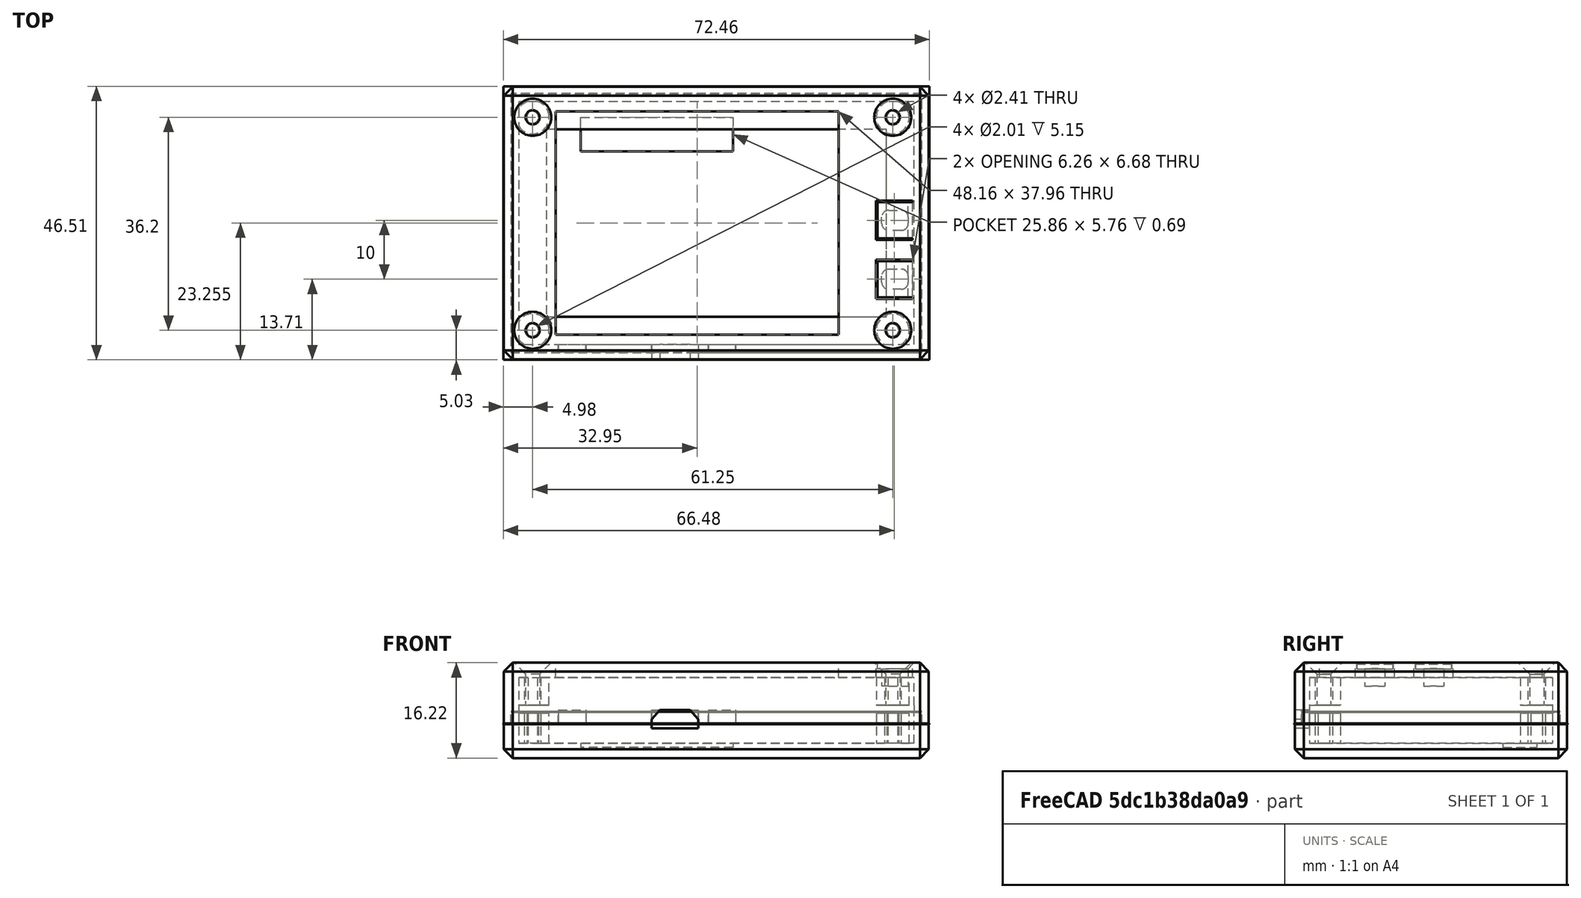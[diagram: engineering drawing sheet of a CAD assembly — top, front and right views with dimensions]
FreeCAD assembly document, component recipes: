
FREECAD ASSEMBLY — COMPONENT RECIPES ("case")

This assembly document has 4 components, labeled P0..P3 below (a component is one placed body or linked part). 2 of them carry a construction recipe — the FreeCAD feature program that regenerates the part from scratch, quoted from this document or its linked companion documents; the rest are supplied as boundary geometry only. No exploded tour is included for this assembly.
COMPONENT P0 — recipe-attached ("Body", modeled in this document).
Construction recipe (the document's own serialized feature program — sketch geometry with constraints, then the solid features built on it; lengths are millimeters unless a unit is written):

FEATURE [Sketcher::SketchObject] Sketch  label="OuterSketch"
  AttachmentOffset = pos=(0,0,-2.81) rot=(0,0,1;0rad)
  FullyConstrained = true
  MapMode = 5
  Placement = pos=(0,0,-2.81) rot=(0,0,1;0rad)
  Support = -> [XY_Plane]
  expr: .AttachmentOffset.Base.z = -(<<Param>>.T_WALL + <<Param>>.S_SIDE + <<Param>>.T_Z)
  expr: Constraints[10] = <<Param>>.T_WALL
  expr: Constraints[11] = <<Param>>.T_WALL
  expr: Constraints[7] = <<Param>>.W_BASE + 2 * (<<Param>>.T_WALL + <<Param>>.S_SIDE + <<Param>>.T_XY)
  expr: Constraints[8] = <<Param>>.H_BASE + 2 * (<<Param>>.T_WALL + <<Param>>.S_SIDE + <<Param>>.T_XY)
  sketch-geometry (4):
    g0: LineSegment StartX=-2.5 StartY=-2.5 StartZ=0 EndX=69.76 EndY=-2.5 EndZ=0
    g1: LineSegment StartX=69.76 StartY=-2.5 StartZ=0 EndX=69.76 EndY=43.81 EndZ=0
    g2: LineSegment StartX=69.76 StartY=43.81 StartZ=0 EndX=-2.5 EndY=43.81 EndZ=0
    g3: LineSegment StartX=-2.5 StartY=43.81 StartZ=0 EndX=-2.5 EndY=-2.5 EndZ=0
  constraints (12):
    c: Coincident(g0,g1)
    c: Coincident(g1,g2)
    c: Coincident(g2,g3)
    c: Horizontal(g0)
    c: Horizontal(g2)
    c: Vertical(g1)
    c: Vertical(g3)
    c: DistanceX(g0,g0) = 72.26
    c: DistanceY(g1,g1) = 46.31
    c: Coincident(g0,g3)
    c: DistanceX(g0,g-1) = 2.5
    c: DistanceY(g0,g-1) = 2.5
FEATURE [PartDesign::Pad] Pad  label="OuterPad"
  Direction = (0,0,1)
  Length = 16.22
  Length2 = 10
  Profile = -> Sketch
  ReferenceAxis = -> Sketch [N_Axis]
  Type = 0
  expr: Length = <<Param>>.D_BASE + 2 * (<<Param>>.T_WALL + <<Param>>.S_SIDE + <<Param>>.T_Z)
FEATURE [PartDesign::Chamfer] Chamfer  label="OuterChamfer"
  Angle = 45
  Base = -> Pad [Face6,Face1,Face5,Face2,Face3,Face4]
  BaseFeature = -> Pad
  ChamferType = 0
  FlipDirection = false
  Size = 1.5
  Size2 = 1
  SupportTransform = false
  UseAllEdges = true
  expr: Size = <<Param>>.R_CORNER
FEATURE [Sketcher::SketchObject] Sketch001  label="InnerSketch"
  AttachmentOffset = pos=(0,0,-0.31) rot=(0,0,1;0rad)
  FullyConstrained = true
  MapMode = 5
  Placement = pos=(0,0,-0.31) rot=(0,0,1;0rad)
  Support = -> [XY_Plane]
  expr: .AttachmentOffset.Base.z = -(<<Param>>.S_SIDE + <<Param>>.T_Z)
  expr: .Constraints.H1 = <<Param>>.H_BASE + 2 * (<<Param>>.S_SIDE + <<Param>>.T_XY)
  expr: .Constraints.W1 = <<Param>>.W_BASE + 2 * (<<Param>>.S_SIDE + <<Param>>.T_XY)
  sketch-geometry (4):
    g0: LineSegment StartX=0 StartY=0 StartZ=0 EndX=67.26 EndY=0 EndZ=0
    g1: LineSegment StartX=67.26 StartY=0 StartZ=0 EndX=67.26 EndY=41.31 EndZ=0
    g2: LineSegment StartX=67.26 StartY=41.31 StartZ=0 EndX=0 EndY=41.31 EndZ=0
    g3: LineSegment StartX=0 StartY=41.31 StartZ=0 EndX=0 EndY=0 EndZ=0
  constraints (11):
    c: Coincident(g0,g1)
    c: Coincident(g1,g2)
    c: Coincident(g2,g3)
    c: Coincident(g3,g0)
    c: Horizontal(g0)
    c: Horizontal(g2)
    c: Vertical(g1)
    c: Vertical(g3)
    c: Coincident(g0,g-1)
    c: DistanceX(g0,g0) = 67.26  'W1'
    c: DistanceY(g1,g1) = 41.31  'H1'
FEATURE [PartDesign::Pocket] Pocket  label="InnerPocket"
  BaseFeature = -> Chamfer
  Direction = (0,0,-1)
  Length = 11.22
  Length2 = 5
  Profile = -> Sketch001
  ReferenceAxis = -> Sketch001 [N_Axis]
  Reversed = true
  Type = 0
  expr: Length = <<Param>>.D_BASE + 2 * (<<Param>>.S_SIDE + <<Param>>.T_Z)
FEATURE [Sketcher::SketchObject] Sketch002  label="UpperScrewHolesSketch"
  AttachmentOffset = pos=(0,0,13.41) rot=(0,0,1;0rad)
  FullyConstrained = true
  MapMode = 5
  Placement = pos=(0,0,13.41) rot=(0,0,1;0rad)
  Support = -> [XY_Plane]
  expr: .AttachmentOffset.Base.z = <<Param>>.D_BASE + <<Param>>.S_SIDE + <<Param>>.T_WALL + <<Param>>.T_Z
  expr: .Constraints.X1 = <<SpacersSketch>>.Constraints.X1
  expr: .Constraints.Y1 = <<SpacersSketch>>.Constraints.Y1
  expr: Constraints[19] = <<Param>>.D_SCREW / 2
  expr: Constraints[8] = <<SpacersSketch>>.Constraints.W1
  expr: Constraints[9] = <<SpacersSketch>>.Constraints.H1
  sketch-geometry (8):
    g0: LineSegment StartX=2.38 StartY=2.43 StartZ=0 EndX=63.63 EndY=2.43 EndZ=0
    g1: LineSegment StartX=63.63 StartY=2.43 StartZ=0 EndX=63.63 EndY=38.63 EndZ=0
    g2: LineSegment StartX=63.63 StartY=38.63 StartZ=0 EndX=2.38 EndY=38.63 EndZ=0
    g3: LineSegment StartX=2.38 StartY=38.63 StartZ=0 EndX=2.38 EndY=2.43 EndZ=0
    g4: Circle CenterX=2.38 CenterY=38.63 CenterZ=0 NormalX=0 NormalY=0 NormalZ=1 AngleXU=0 Radius=1.125
    g5: Circle CenterX=63.63 CenterY=38.63 CenterZ=0 NormalX=0 NormalY=0 NormalZ=1 AngleXU=0 Radius=1.125
    g6: Circle CenterX=63.63 CenterY=2.43 CenterZ=0 NormalX=0 NormalY=0 NormalZ=1 AngleXU=0 Radius=1.125
    g7: Circle CenterX=2.38 CenterY=2.43 CenterZ=0 NormalX=0 NormalY=0 NormalZ=1 AngleXU=0 Radius=1.125
  constraints (20):
    c: Coincident(g0,g1)
    c: Coincident(g1,g2)
    c: Coincident(g2,g3)
    c: Coincident(g3,g0)
    c: Horizontal(g0)
    c: Horizontal(g2)
    c: Vertical(g1)
    c: Vertical(g3)
    c: DistanceX(g0,g0) = 61.25
    c: DistanceY(g1,g1) = 36.2
    c: DistanceX(g-1,g0) = 2.38  'X1'
    c: DistanceY(g-1,g0) = 2.43  'Y1'
    c: Coincident(g4,g2)
    c: Coincident(g5,g1)
    c: Coincident(g6,g0)
    c: Coincident(g7,g0)
    c: Equal(g4,g7)
    c: Equal(g7,g6)
    c: Equal(g6,g5)
    c: Radius(g4) = 1.125
FEATURE [Sketcher::SketchObject] Sketch003  label="SpacersSketch"
  AttachmentOffset = pos=(0,0,-0.31) rot=(0,0,1;0rad)
  FullyConstrained = true
  MapMode = 5
  Placement = pos=(0,0,-0.31) rot=(0,0,1;0rad)
  Support = -> [XY_Plane]
  expr: .AttachmentOffset.Base.z = <<InnerSketch>>.Placement.Base.z
  expr: .Constraints.H1 = 36.2 mm
  expr: .Constraints.W1 = 61.25 mm
  expr: .Constraints.X1 = 2.05 mm + <<Param>>.S_SIDE + <<Param>>.T_XY
  expr: .Constraints.Y1 = 2.1 mm + <<Param>>.S_SIDE + <<Param>>.T_XY
  expr: Constraints[19] = 2.8 mm
  sketch-geometry (8):
    g0: LineSegment StartX=2.38 StartY=2.43 StartZ=0 EndX=63.63 EndY=2.43 EndZ=0
    g1: LineSegment StartX=63.63 StartY=2.43 StartZ=0 EndX=63.63 EndY=38.63 EndZ=0
    g2: LineSegment StartX=63.63 StartY=38.63 StartZ=0 EndX=2.38 EndY=38.63 EndZ=0
    g3: LineSegment StartX=2.38 StartY=38.63 StartZ=0 EndX=2.38 EndY=2.43 EndZ=0
    g4: Circle CenterX=2.38 CenterY=38.63 CenterZ=0 NormalX=0 NormalY=0 NormalZ=1 AngleXU=0 Radius=2.8
    g5: Circle CenterX=63.63 CenterY=38.63 CenterZ=0 NormalX=0 NormalY=0 NormalZ=1 AngleXU=0 Radius=2.8
    g6: Circle CenterX=63.63 CenterY=2.43 CenterZ=0 NormalX=0 NormalY=0 NormalZ=1 AngleXU=0 Radius=2.8
    g7: Circle CenterX=2.38 CenterY=2.43 CenterZ=0 NormalX=0 NormalY=0 NormalZ=1 AngleXU=0 Radius=2.8
  constraints (20):
    c: Coincident(g0,g1)
    c: Coincident(g1,g2)
    c: Coincident(g2,g3)
    c: Coincident(g3,g0)
    c: Horizontal(g0)
    c: Horizontal(g2)
    c: Vertical(g1)
    c: Vertical(g3)
    c: DistanceX(g0,g0) = 61.25  'W1'
    c: DistanceY(g1,g1) = 36.2  'H1'
    c: DistanceX(g-1,g0) = 2.38  'X1'
    c: DistanceY(g-1,g0) = 2.43  'Y1'
    c: Coincident(g4,g2)
    c: Coincident(g5,g1)
    c: Coincident(g6,g0)
    c: Coincident(g7,g0)
    c: Equal(g4,g7)
    c: Equal(g7,g6)
    c: Equal(g6,g5)
    c: Radius(g4) = 2.8
FEATURE [PartDesign::Pad] Pad001  label="SpacersPad"
  BaseFeature = -> Pocket
  Direction = (0,0,1)
  Length = 11.22
  Length2 = 10
  Profile = -> Sketch003
  ReferenceAxis = -> Sketch003 [N_Axis]
  Type = 0
  expr: Length = <<InnerPocket>>.Length
FEATURE [PartDesign::SubShapeBinder] Binder  label="InnerSketchBinder"
  BindCopyOnChange = 0
  BindMode = 0
  ClaimChildren = false
  Context = -> Body [Binder.]
  Fuse = false
  MakeFace = true
  OffsetFill = false
  OffsetIntersection = false
  OffsetJoinType = 0
  OffsetOpenResult = false
  PartialLoad = false
  Placement = pos=(0,0,6.47) rot=(0,0,1;0rad)
  Relative = true
  Support = -> [Pocket[Sketch001.]]
  _Version = 2
  expr: .Placement.Base.z = <<InnerPocket>>.Length - <<Param>>.S_SIDE - <<Param>>.Y_TOP
FEATURE [Sketcher::SketchObject] Sketch005  label="ScreenBaseSketch"
  AttachmentOffset = pos=(0,0,6.47) rot=(0,0,1;0rad)
  FullyConstrained = true
  MapMode = 5
  Placement = pos=(0,0,6.47) rot=(0,0,1;0rad)
  Support = -> [XY_Plane]
  expr: .AttachmentOffset.Base.z = <<InnerSketchBinder>>.Placement.Base.z
  expr: Constraints[19] = <<InnerSketch>>.Constraints.W1
  expr: Constraints[20] = <<InnerSketch>>.Constraints.H1
  expr: Constraints[24] = <<UpperScrewHolesSketch>>.Constraints.X1 + 0.9 mm
  expr: Constraints[8] = <<Param>>.W_SCREEN + 2 * <<Param>>.T_XY
  expr: Constraints[9] = <<Param>>.H_SCREEN + 2 * <<Param>>.T_XY
  sketch-geometry (10):
    g0: LineSegment StartX=6.27 StartY=1.675 StartZ=0 EndX=54.43 EndY=1.675 EndZ=0
    g1: LineSegment StartX=54.43 StartY=1.675 StartZ=0 EndX=54.43 EndY=39.635 EndZ=0
    g2: LineSegment StartX=54.43 StartY=39.635 StartZ=0 EndX=6.27 EndY=39.635 EndZ=0
    g3: LineSegment StartX=6.27 StartY=39.635 StartZ=0 EndX=6.27 EndY=1.675 EndZ=0
    g4: LineSegment StartX=0 StartY=0 StartZ=0 EndX=67.26 EndY=0 EndZ=0
    g5: LineSegment StartX=67.26 StartY=0 StartZ=0 EndX=67.26 EndY=41.31 EndZ=0
    g6: LineSegment StartX=67.26 StartY=41.31 StartZ=0 EndX=0 EndY=41.31 EndZ=0
    g7: LineSegment StartX=0 StartY=41.31 StartZ=0 EndX=0 EndY=0 EndZ=0
    g8: GeomPoint X=33.63 Y=20.655 Z=0
    g9: GeomPoint X=30.35 Y=20.655 Z=0
  constraints (25):
    c: Coincident(g0,g1)
    c: Coincident(g1,g2)
    c: Coincident(g2,g3)
    c: Coincident(g3,g0)
    c: Horizontal(g0)
    c: Horizontal(g2)
    c: Vertical(g1)
    c: Vertical(g3)
    c: DistanceX(g0,g0) = 48.16
    c: DistanceY(g1,g1) = 37.96
    c: Coincident(g4,g5)
    c: Coincident(g5,g6)
    c: Coincident(g6,g7)
    c: Coincident(g7,g4)
    c: Horizontal(g4)
    c: Horizontal(g6)
    c: Vertical(g5)
    c: Vertical(g7)
    c: Coincident(g4,g-1)
    c: DistanceX(g4,g4) = 67.26
    c: DistanceY(g5,g5) = 41.31
    c: Symmetric(g4,g5,g8)
    c: Symmetric(g0,g1,g9)
    c: Horizontal(g9,g8)
    c: DistanceX(g9,g8) = 3.28
FEATURE [PartDesign::Hole] Hole  label="UpperScrewHoles"
  BaseFeature = -> Pad001
  CustomThreadClearance = 0
  Depth = 7.31
  DepthType = 0
  Diameter = 2.41
  DrillForDepth = false
  DrillPoint = 0
  DrillPointAngle = 118
  HoleCutCountersinkAngle = 90
  HoleCutCustomValues = false
  HoleCutDepth = 0
  HoleCutDiameter = 6.3
  HoleCutType = 2
  ModelThread = false
  Profile = -> Sketch002
  Tapered = false
  TaperedAngle = 90
  ThreadClass = 0
  ThreadDepth = 7.31
  ThreadDepthType = 0
  ThreadDirection = 0
  ThreadFit = 1
  ThreadSize = 0
  ThreadType = 0
  Threaded = false
  UseCustomThreadClearance = false
  expr: Depth = <<Param>>.T_WALL + <<Param>>.S_SIDE + <<Param>>.T_Z + <<Param>>.Y_TOP
  expr: Diameter = <<Param>>.D_SCREW + 2 * <<Param>>.T_XY
FEATURE [PartDesign::Hole] Hole001  label="InnerScrewHoles"
  BaseFeature = -> Hole
  CustomThreadClearance = 0
  Depth = 13.72
  DepthType = 0
  Diameter = 2.01
  DrillForDepth = false
  DrillPoint = 0
  DrillPointAngle = 118
  HoleCutCountersinkAngle = 90
  HoleCutCustomValues = false
  HoleCutDepth = 0
  HoleCutDiameter = 6.1
  HoleCutType = 0
  ModelThread = false
  Profile = -> Sketch002
  Tapered = false
  TaperedAngle = 90
  ThreadClass = 0
  ThreadDepth = 13.72
  ThreadDepthType = 0
  ThreadDirection = 0
  ThreadFit = 0
  ThreadSize = 0
  ThreadType = 0
  Threaded = false
  UseCustomThreadClearance = false
  expr: Depth = <<Param>>.T_WALL + <<InnerPocket>>.Length
  expr: Diameter = <<Param>>.D_SCREW - 0.4 mm + 2 * <<Param>>.T_XY
FEATURE [PartDesign::Pocket] Pocket002  label="PcbPocket"
  BaseFeature = -> Hole001
  Direction = (0,0,-1)
  Length = 1.32
  Length2 = 5
  Profile = -> Binder
  Type = 0
  expr: Length = <<Param>>.T_PCB + 2 * <<Param>>.T_Z
FEATURE [PartDesign::Pocket] Pocket003  label="ScreenBasePocket"
  BaseFeature = -> Pocket002
  Direction = (0,0,-1)
  Length = 5
  Length2 = 5
  Profile = -> Sketch005
  ReferenceAxis = -> Sketch005 [N_Axis]
  Reversed = true
  Type = 1
FEATURE [Sketcher::SketchObject] Sketch006  label="TasterSketch"
  AttachmentOffset = pos=(0,0,5.33) rot=(0,0,1;0rad)
  FullyConstrained = true
  MapMode = 5
  Placement = pos=(0,0,5.33) rot=(0,0,1;0rad)
  Support = -> [XY_Plane]
  expr: .AttachmentOffset.Base.z = <<InnerSketchBinder>>.Placement.Base.z - <<Param>>.T_PCB + <<Param>>.T_Z
  expr: Constraints[10] = 4.5 mm + 2 * <<Param>>.T_XY
  expr: Constraints[11] = 1.2 mm + <<Param>>.T_XY
  expr: Constraints[23] = 32 mm + <<Param>>.S_SIDE
  expr: Constraints[9] = 6.5 mm + <<Param>>.S_SIDE
  sketch-geometry (8):
    g0: LineSegment StartX=6.75 StartY=0 StartZ=0 EndX=11.41 EndY=0 EndZ=0
    g1: LineSegment StartX=11.41 StartY=0 StartZ=0 EndX=11.41 EndY=-1.28 EndZ=0
    g2: LineSegment StartX=11.41 StartY=-1.28 StartZ=0 EndX=6.75 EndY=-1.28 EndZ=0
    g3: LineSegment StartX=6.75 StartY=-1.28 StartZ=0 EndX=6.75 EndY=0 EndZ=0
    g4: LineSegment StartX=32.25 StartY=0 StartZ=0 EndX=36.91 EndY=0 EndZ=0
    g5: LineSegment StartX=36.91 StartY=0 StartZ=0 EndX=36.91 EndY=-1.28 EndZ=0
    g6: LineSegment StartX=36.91 StartY=-1.28 StartZ=0 EndX=32.25 EndY=-1.28 EndZ=0
    g7: LineSegment StartX=32.25 StartY=-1.28 StartZ=0 EndX=32.25 EndY=0 EndZ=0
  constraints (24):
    c: Coincident(g0,g1)
    c: Coincident(g1,g2)
    c: Coincident(g2,g3)
    c: Coincident(g3,g0)
    c: Horizontal(g0)
    c: Horizontal(g2)
    c: Vertical(g1)
    c: Vertical(g3)
    c: PointOnObject(g0,g-1)
    c: DistanceX(g0) = 6.75
    c: DistanceX(g0,g0) = 4.66
    c: DistanceY(g1,g1) = 1.28
    c: Coincident(g4,g5)
    c: Coincident(g5,g6)
    c: Coincident(g6,g7)
    c: Coincident(g7,g4)
    c: Horizontal(g4)
    c: Horizontal(g6)
    c: Vertical(g5)
    c: Vertical(g7)
    c: PointOnObject(g4,g-1)
    c: Horizontal(g1,g6)
    c: Equal(g4,g0)
    c: DistanceX(g4) = 32.25
FEATURE [Sketcher::SketchObject] Sketch007  label="UsbSketch"
  FullyConstrained = true
  MapMode = 5
  Placement = pos=(0,0,0) rot=(1,0,0;1.5708rad)
  Support = -> [XZ_Plane]
  expr: .Constraints.H1 = 3 mm + 2 * <<Param>>.T_Z
  expr: .Constraints.W1 = 7.8 mm + 2 * <<Param>>.T_XY
  expr: .Constraints.X1 = 22.34 mm + <<Param>>.S_SIDE
  expr: .Constraints.Y1 = <<InnerSketchBinder>>.Placement.Base.z - <<Param>>.T_PCB + 0.1 mm
  expr: Constraints[22] = 5 mm + 2 * <<Param>>.T_XY
  expr: Constraints[27] = 1.5 mm
  sketch-geometry (10):
    g0: LineSegment StartX=29.15 StartY=5.37 StartZ=0 EndX=23.99 EndY=5.37 EndZ=0
    g1: LineSegment StartX=23.99 StartY=5.37 StartZ=0 EndX=22.59 EndY=3.75 EndZ=0
    g2: LineSegment StartX=22.59 StartY=3.75 StartZ=0 EndX=22.59 EndY=2.25 EndZ=0
    g3: LineSegment StartX=22.59 StartY=2.25 StartZ=0 EndX=30.55 EndY=2.25 EndZ=0
    g4: LineSegment StartX=30.55 StartY=2.25 StartZ=0 EndX=30.55 EndY=3.75 EndZ=0
    g5: LineSegment StartX=30.55 StartY=3.75 StartZ=0 EndX=29.15 EndY=5.37 EndZ=0
    g6: LineSegment StartX=22.59 StartY=3.75 StartZ=0 EndX=23.99 EndY=3.75 EndZ=0
    g7: LineSegment StartX=23.99 StartY=3.75 StartZ=0 EndX=29.15 EndY=3.75 EndZ=0
    g8: LineSegment StartX=29.15 StartY=3.75 StartZ=0 EndX=30.55 EndY=3.75 EndZ=0
    g9: GeomPoint X=22.59 Y=5.37 Z=0
  constraints (28):
    c: Horizontal(g0)
    c: Coincident(g0,g1)
    c: Coincident(g1,g2)
    c: Vertical(g2)
    c: Coincident(g2,g3)
    c: Horizontal(g3)
    c: Coincident(g3,g4)
    c: Vertical(g4)
    c: Coincident(g4,g5)
    c: Coincident(g5,g0)
    c: Horizontal(g1,g4)
    c: Coincident(g6,g1)
    c: Horizontal(g6)
    c: Coincident(g7,g6)
    c: Horizontal(g7)
    c: Coincident(g8,g7)
    c: Coincident(g8,g4)
    c: Vertical(g0,g7)
    c: Vertical(g0,g6)
    c: Equal(g8,g6)
    c: DistanceY(g3,g0) = 3.12  'H1'
    c: DistanceX(g3,g3) = 7.96  'W1'
    c: DistanceX(g0,g0) = 5.16
    c: Vertical(g9,g1)
    c: Horizontal(g9,g0)
    c: DistanceX(g9) = 22.59  'X1'
    c: DistanceY(g9) = 5.37  'Y1'
    c: DistanceY(g2,g2) = 1.5
FEATURE [Sketcher::SketchObject] Sketch008  label="ButtonSketch"
  AttachmentOffset = pos=(0,0,0.25) rot=(0,0,1;0rad)
  FullyConstrained = true
  MapMode = 5
  Placement = pos=(0,0,0.25) rot=(0,0,1;0rad)
  Support = -> [XY_Plane]
  expr: .AttachmentOffset.Base.z = <<Param>>.S_SIDE
  expr: .Constraints.H1 = 6 mm + 2 * <<Param>>.T_XY
  expr: .Constraints.W1 = 6 mm
  expr: .Constraints.X1 = <<InnerSketch>>.Constraints.W1 - <<Param>>.S_SIDE
  expr: .Constraints.Y1 = 7.7 mm + <<Param>>.S_SIDE + <<Param>>.T_XY
  expr: .Constraints.Y2 = .Constraints.H1 + 0.1 mm + 2 * <<Param>>.T_XY
  expr: Constraints[25] = .Constraints.Y2
  sketch-geometry (9):
    g0: LineSegment StartX=60.75 StartY=14.45 StartZ=0 EndX=67.01 EndY=14.45 EndZ=0
    g1: LineSegment StartX=67.01 StartY=14.45 StartZ=0 EndX=67.01 EndY=14.19 EndZ=0
    g2: LineSegment StartX=67.01 StartY=7.77 StartZ=0 EndX=60.75 EndY=7.77 EndZ=0
    g3: LineSegment StartX=60.75 StartY=7.77 StartZ=0 EndX=60.75 EndY=14.45 EndZ=0
    g4: LineSegment StartX=61.01 StartY=14.19 StartZ=0 EndX=67.01 EndY=14.19 EndZ=0
    g5: LineSegment StartX=67.01 StartY=8.03 StartZ=0 EndX=61.01 EndY=8.03 EndZ=0
    g6: LineSegment StartX=61.01 StartY=8.03 StartZ=0 EndX=61.01 EndY=14.19 EndZ=0
    g7: LineSegment StartX=67.01 StartY=8.03 StartZ=0 EndX=67.01 EndY=7.77 EndZ=0
    g8: LineSegment StartX=61.01 StartY=8.03 StartZ=0 EndX=60.75 EndY=8.03 EndZ=0
  constraints (29):
    c: Coincident(g0,g1)
    c: Coincident(g7,g2)
    c: Coincident(g2,g3)
    c: Coincident(g3,g0)
    c: Horizontal(g0)
    c: Horizontal(g2)
    c: Vertical(g1)
    c: Vertical(g3)
    c: Coincident(g5,g6)
    c: Coincident(g6,g4)
    c: Horizontal(g4)
    c: Horizontal(g5)
    c: Vertical(g6)
    c: Coincident(g4,g1)
    c: Coincident(g5,g7)
    c: Vertical(g1,g5)
    c: Coincident(g8,g5)
    c: PointOnObject(g8,g3)
    c: Horizontal(g8)
    c: DistanceY(g6,g6) = 6.16  'H1'
    c: DistanceX(g5,g5) = 6  'W1'
    c: Vertical(g7)
    c: DistanceY(g2,g1) = 6.42  'Y2'
    c: DistanceX(g5) = 67.01  'X1'
    c: DistanceY(g5) = 8.03  'Y1'
    c: DistanceY(g5,g0) = 6.42
    c: Equal(g7,g8)
    c: DistanceY(g3,g3) = 6.68  'H2'
    c: DistanceX(g2,g2) = 6.26  'W2'
FEATURE [Sketcher::SketchObject] Sketch009  label="ButtonPeerSketch"
  AttachmentOffset = pos=(0,0,13.41) rot=(0,0,1;0rad)
  FullyConstrained = false
  MapMode = 5
  Placement = pos=(0,0,13.41) rot=(0,0,1;0rad)
  Support = -> [XY_Plane]
  expr: .AttachmentOffset.Base.z = <<OuterSketch>>.Placement.Base.z + <<OuterPad>>.Length
  expr: Constraints[10] = <<ButtonSketch>>.Constraints.W1
  expr: Constraints[11] = <<ButtonSketch>>.Constraints.H1
  expr: Constraints[34] = 3.4 mm
  expr: Constraints[36] = 4.5 mm
  expr: Constraints[8] = <<ButtonSketch>>.Constraints.X1 - <<Param>>.S_SIDE - 0.5 mm
  expr: Constraints[9] = <<ButtonSketch>>.Constraints.Y1
  sketch-geometry (15):
    g0: LineSegment StartX=60.26 StartY=14.19 StartZ=0 EndX=66.26 EndY=14.19 EndZ=0
    g1: LineSegment StartX=66.26 StartY=14.19 StartZ=0 EndX=66.26 EndY=8.03 EndZ=0
    g2: LineSegment StartX=66.26 StartY=8.03 StartZ=0 EndX=60.26 EndY=8.03 EndZ=0
    g3: LineSegment StartX=60.26 StartY=8.03 StartZ=0 EndX=60.26 EndY=14.19 EndZ=0
    g4: ArcOfCircle CenterX=62.9093 CenterY=11.6607 CenterZ=0 NormalX=0 NormalY=0 NormalZ=1 AngleXU=0 Radius=1.14926 StartAngle=1.5708 EndAngle=3.14159
    g5: LineSegment StartX=62.9093 StartY=12.81 StartZ=0 EndX=65.1107 EndY=12.81 EndZ=0
    g6: ArcOfCircle CenterX=65.1107 CenterY=11.6607 CenterZ=0 NormalX=0 NormalY=0 NormalZ=1 AngleXU=0 Radius=1.14926 StartAngle=0 EndAngle=1.5708
    g7: LineSegment StartX=66.26 StartY=11.6607 StartZ=0 EndX=66.26 EndY=10.5593 EndZ=0
    g8: ArcOfCircle CenterX=65.1107 CenterY=10.5593 CenterZ=0 NormalX=0 NormalY=0 NormalZ=1 AngleXU=0 Radius=1.14926 StartAngle=4.71239 EndAngle=6.28319
    g9: LineSegment StartX=65.1107 StartY=9.41 StartZ=0 EndX=62.9093 EndY=9.41 EndZ=0
    g10: ArcOfCircle CenterX=62.9093 CenterY=10.5593 CenterZ=0 NormalX=0 NormalY=0 NormalZ=1 AngleXU=0 Radius=1.14926 StartAngle=3.14159 EndAngle=4.71239
    g11: LineSegment StartX=61.76 StartY=10.5593 StartZ=0 EndX=61.76 EndY=11.6607 EndZ=0
    g12: GeomPoint X=61.76 Y=12.81 Z=0
    g13: GeomPoint X=66.26 Y=9.41 Z=0
    g14: LineSegment StartX=64.01 StartY=11.11 StartZ=0 EndX=66.26 EndY=11.11 EndZ=0
  constraints (37):
    c: Coincident(g0,g1)
    c: Coincident(g1,g2)
    c: Coincident(g2,g3)
    c: Coincident(g3,g0)
    c: Horizontal(g0)
    c: Horizontal(g2)
    c: Vertical(g1)
    c: Vertical(g3)
    c: DistanceX(g1) = 66.26
    c: DistanceY(g1) = 8.03
    c: DistanceX(g2,g2) = 6
    c: DistanceY(g1,g1) = 6.16
    c: Tangent(g4,g5) = 1.5708
    c: Tangent(g5,g6) = 1.5708
    c: Tangent(g6,g7) = 1.5708
    c: Tangent(g7,g8) = 1.5708
    c: Tangent(g8,g9) = 1.5708
    c: Tangent(g9,g10) = 1.5708
    c: Tangent(g10,g11) = 1.5708
    c: Tangent(g11,g4) = 1.5708
    c: Horizontal(g5)
    c: Horizontal(g9)
    c: Vertical(g7)
    c: Vertical(g11)
    c: Equal(g4,g6)
    c: Equal(g6,g8)
    c: Equal(g8,g10)
    c: PointOnObject(g12,g5)
    c: PointOnObject(g12,g11)
    c: PointOnObject(g13,g7)
    c: PointOnObject(g13,g9)
    c: Horizontal(g14)
    c: Symmetric(g4,g8,g14)
    c: Symmetric(g1,g0,g14)
    c: DistanceY(g9,g4) = 3.4
    c: Vertical(g6,g0)
    c: DistanceX(g10,g7) = 4.5
FEATURE [Sketcher::SketchObject] Sketch011  label="InnerUsbSketch"
  FullyConstrained = true
  MapMode = 5
  Placement = pos=(0,0,0) rot=(1,0,0;1.5708rad)
  Support = -> [XZ_Plane]
  expr: Constraints[10] = <<UsbSketch>>.Constraints.W1
  expr: Constraints[11] = <<UsbSketch>>.Constraints.H1
  expr: Constraints[8] = <<UsbSketch>>.Constraints.X1
  expr: Constraints[9] = <<UsbSketch>>.Constraints.Y1
  sketch-geometry (4):
    g0: LineSegment StartX=22.59 StartY=5.37 StartZ=0 EndX=30.55 EndY=5.37 EndZ=0
    g1: LineSegment StartX=30.55 StartY=5.37 StartZ=0 EndX=30.55 EndY=2.25 EndZ=0
    g2: LineSegment StartX=30.55 StartY=2.25 StartZ=0 EndX=22.59 EndY=2.25 EndZ=0
    g3: LineSegment StartX=22.59 StartY=2.25 StartZ=0 EndX=22.59 EndY=5.37 EndZ=0
  constraints (12):
    c: Coincident(g0,g1)
    c: Coincident(g1,g2)
    c: Coincident(g2,g3)
    c: Coincident(g3,g0)
    c: Horizontal(g0)
    c: Horizontal(g2)
    c: Vertical(g1)
    c: Vertical(g3)
    c: DistanceX(g0) = 22.59
    c: DistanceY(g0) = 5.37
    c: DistanceX(g0,g0) = 7.96
    c: DistanceY(g1,g1) = 3.12
FEATURE [Sketcher::SketchObject] Sketch012  label="ButtonCarveSketch"
  AttachmentOffset = pos=(0,0,-8.03) rot=(0,0,1;0rad)
  FullyConstrained = true
  MapMode = 5
  Placement = pos=(0,8.03,1.8e-15) rot=(1,0,0;1.5708rad)
  Support = -> [XZ_Plane]
  expr: .AttachmentOffset.Base.z = -<<ButtonSketch>>.Constraints.Y1
  expr: .Constraints.Y1 = <<InnerPocket>>.Length - <<Param>>.S_SIDE - <<Param>>.T_Z
  expr: .Constraints.Y2 = <<InnerPocket>>.Length - <<Param>>.S_SIDE - 2 * <<Param>>.T_Z + <<Param>>.T_WALL - <<Param>>.T_BUTTON
  expr: .Constraints.Y3 = <<InnerPocket>>.Length - <<Param>>.S_SIDE - 2 * <<Param>>.T_Z + <<Param>>.T_WALL - <<Param>>.T_LAYER
  expr: Constraints[10] = <<ButtonSketch>>.Constraints.X1
  expr: Constraints[14] = <<ButtonSketch>>.Constraints.W2
  sketch-geometry (5):
    g0: LineSegment StartX=66.21 StartY=12.35 StartZ=0 EndX=60.75 EndY=12.35 EndZ=0
    g1: LineSegment StartX=60.75 StartY=12.35 StartZ=0 EndX=60.75 EndY=10.91 EndZ=0
    g2: LineSegment StartX=60.75 StartY=10.91 StartZ=0 EndX=67.01 EndY=10.91 EndZ=0
    g3: LineSegment StartX=67.01 StartY=10.91 StartZ=0 EndX=67.01 EndY=13.15 EndZ=0
    g4: LineSegment StartX=67.01 StartY=13.15 StartZ=0 EndX=66.21 EndY=12.35 EndZ=0
  constraints (15):
    c: Horizontal(g0)
    c: Coincident(g0,g1)
    c: Vertical(g1)
    c: Coincident(g1,g2)
    c: Horizontal(g2)
    c: Coincident(g2,g3)
    c: Vertical(g3)
    c: Coincident(g3,g4)
    c: Coincident(g4,g0)
    c: Angle(g4,g3) = 0.785398
    c: DistanceX(g2) = 67.01
    c: DistanceY(g0) = 12.35  'Y2'
    c: DistanceY(g3) = 13.15  'Y3'
    c: DistanceY(g1) = 10.91  'Y1'
    c: DistanceX(g2,g2) = 6.26
FEATURE [Sketcher::SketchObject] Sketch013  label="PinHeaderSketch"
  FullyConstrained = true
  MapMode = 5
  Support = -> [XY_Plane]
  expr: Constraints[10] = 5.1 mm + 2 * (<<Param>>.S_SIDE + <<Param>>.T_XY)
  expr: Constraints[11] = 25.2 mm + 2 * (<<Param>>.S_SIDE + <<Param>>.T_XY)
  expr: Constraints[8] = 10.9 mm - <<Param>>.S_SIDE - <<Param>>.T_XY
  expr: Constraints[9] = 33.2 mm - <<Param>>.S_SIDE - <<Param>>.T_XY
  sketch-geometry (4):
    g0: LineSegment StartX=10.57 StartY=38.63 StartZ=0 EndX=36.43 EndY=38.63 EndZ=0
    g1: LineSegment StartX=36.43 StartY=38.63 StartZ=0 EndX=36.43 EndY=32.87 EndZ=0
    g2: LineSegment StartX=36.43 StartY=32.87 StartZ=0 EndX=10.57 EndY=32.87 EndZ=0
    g3: LineSegment StartX=10.57 StartY=32.87 StartZ=0 EndX=10.57 EndY=38.63 EndZ=0
  constraints (12):
    c: Coincident(g0,g1)
    c: Coincident(g1,g2)
    c: Coincident(g2,g3)
    c: Coincident(g3,g0)
    c: Horizontal(g0)
    c: Horizontal(g2)
    c: Vertical(g1)
    c: Vertical(g3)
    c: DistanceX(g2) = 10.57
    c: DistanceY(g2) = 32.87
    c: DistanceY(g1,g1) = 5.76
    c: DistanceX(g0,g0) = 25.86
FEATURE [PartDesign::Pocket] Pocket009  label="PinHeaderPocket"
  BaseFeature = -> Pocket003
  Direction = (0,0,-1)
  Length = 1
  Length2 = 5
  Profile = -> Sketch013
  ReferenceAxis = -> Sketch013 [N_Axis]
  Type = 0
FEATURE [PartDesign::Pocket] Pocket004  label="TasterPocket"
  BaseFeature = -> Pocket009
  Direction = (0,0,-1)
  Length = 2.47
  Length2 = 5
  Profile = -> Sketch006
  ReferenceAxis = -> Sketch006 [N_Axis]
  Type = 0
  expr: Length = 2.35 mm + 2 * <<Param>>.T_Z
FEATURE [PartDesign::Pocket] Pocket005  label="UsbPocket"
  BaseFeature = -> Pocket004
  Direction = (0,1,2e-16)
  Length = 5
  Length2 = 5
  Profile = -> Sketch007
  ReferenceAxis = -> Sketch007 [N_Axis]
  Reversed = true
  Type = 1
FEATURE [PartDesign::Pocket] Pocket007  label="InnerUsbPocket"
  BaseFeature = -> Pocket005
  Direction = (0,1,2e-16)
  Length = 1.33
  Length2 = 5
  Profile = -> Sketch011
  ReferenceAxis = -> Sketch011 [N_Axis]
  Reversed = true
  Type = 0
  expr: Length = <<Param>>.T_WALL / 2 + <<Param>>.T_XY
FEATURE [PartDesign::Pocket] Pocket006  label="ButtonPocket"
  BaseFeature = -> Pocket007
  Direction = (0,0,-1)
  Length = 5
  Length2 = 5
  Profile = -> Sketch008
  ReferenceAxis = -> Sketch008 [N_Axis]
  Reversed = true
  Type = 1
FEATURE [PartDesign::Pocket] Pocket008  label="ButtonCarvePocket"
  BaseFeature = -> Pocket006
  Direction = (0,1,2e-16)
  Length = 6.16
  Length2 = 5
  Profile = -> Sketch012
  ReferenceAxis = -> Sketch012 [N_Axis]
  Type = 0
  expr: Length = <<ButtonSketch>>.Constraints.H1
FEATURE [PartDesign::Pad] Pad002  label="ButtonPeerPad"
  BaseFeature = -> Pocket008
  Direction = (0,0,1)
  Length = 4
  Length2 = 10
  Profile = -> Sketch009
  ReferenceAxis = -> Sketch009 [N_Axis]
  Reversed = true
  Type = 0
  expr: Length = <<Param>>.T_WALL + <<Param>>.S_SIDE + 1.25 mm
FEATURE [PartDesign::LinearPattern] LinearPattern  label="ButtonLinearPattern"
  BaseFeature = -> Pad002
  Direction = -> Y_Axis
  Length = 10
  Occurrences = 2
  Originals = -> [Pocket006,Pocket008,Pad002]
FEATURE [PartDesign::Body] Body
  Group = -> [Sketch,Pad,Chamfer,Sketch001,Pocket,Sketch002,Sketch003,Pad001,Hole,Hole001,Binder,Pocket002,Sketch005,Pocket003,Sketch006,Sketch013,Pocket009,Pocket004,Sketch007,Pocket005,Sketch008,Sketch011,Pocket007,Pocket006,Sketch009,Sketch012,Pocket008,Pad002,LinearPattern]
  Origin = -> Origin
  Tip = -> LinearPattern
COMPONENT P1 — recipe-attached ("Gap", modeled in this document).
Construction recipe (the document's own serialized feature program — sketch geometry with constraints, then the solid features built on it; lengths are millimeters unless a unit is written):

FEATURE [Sketcher::SketchObject] Sketch010  label="GapSketch"
  AttachmentOffset = pos=(0,0,-20.655) rot=(0,0,1;0rad)
  FullyConstrained = true
  MapMode = 5
  Placement = pos=(0,20.655,4.6e-15) rot=(1,0,0;1.5708rad)
  Support = -> [XZ_Plane001]
  expr: .AttachmentOffset.Base.z = -<<InnerSketch>>.Constraints.H1 / 2
  expr: .Constraints.Y1 = <<InnerSketchBinder>>.Placement.Base.z - <<Param>>.S_SIDE - <<Param>>.T_PCB + <<Param>>.T_Z
  expr: .Constraints.Y2 = .Constraints.Y1 - 2 * <<Param>>.T_Z
  expr: Constraints[16] = -<<Param>>.T_WALL - 0.1 mm
  expr: Constraints[26] = <<Param>>.T_XY
  expr: Constraints[27] = <<Param>>.H_LATCH
  sketch-geometry (9):
    g0: LineSegment StartX=4.725 StartY=5.08 StartZ=0 EndX=-1.355 EndY=5.08 EndZ=0
    g1: LineSegment StartX=-1.355 StartY=5.08 StartZ=0 EndX=-1.355 EndY=3.08 EndZ=0
    g2: LineSegment StartX=-1.355 StartY=3.08 StartZ=0 EndX=-2.6 EndY=3.08 EndZ=0
    g3: LineSegment StartX=-2.6 StartY=3.08 StartZ=0 EndX=-2.6 EndY=2.96 EndZ=0
    g4: LineSegment StartX=-2.6 StartY=2.96 StartZ=0 EndX=-1.275 EndY=2.96 EndZ=0
    g5: LineSegment StartX=-1.275 StartY=2.96 StartZ=0 EndX=-1.275 EndY=4.96 EndZ=0
    g6: LineSegment StartX=-1.275 StartY=4.96 StartZ=0 EndX=4.725 EndY=4.96 EndZ=0
    g7: LineSegment StartX=4.725 StartY=4.96 StartZ=0 EndX=4.725 EndY=5.08 EndZ=0
    g8: LineSegment StartX=-1.275 StartY=2.96 StartZ=0 EndX=0.05 EndY=2.96 EndZ=0
  constraints (28):
    c: Horizontal(g0)
    c: Coincident(g0,g1)
    c: Vertical(g1)
    c: Coincident(g1,g2)
    c: Horizontal(g2)
    c: Coincident(g2,g3)
    c: Coincident(g3,g4)
    c: Horizontal(g4)
    c: Coincident(g4,g5)
    c: Vertical(g5)
    c: Coincident(g5,g6)
    c: Horizontal(g6)
    c: Coincident(g6,g7)
    c: Coincident(g7,g0)
    c: Vertical(g7)
    c: Vertical(g3)
    c: DistanceX(g2) = -2.6
    c: DistanceY(g0) = 5.08  'Y1'
    c: DistanceY(g5) = 4.96  'Y2'
    c: Equal(g1,g5)
    c: DistanceX(g6,g6) = 6
    c: Horizontal(g8)
    c: DistanceX(g8,g8) = 1.325  'W1'
    c: Equal(g4,g8)
    c: DistanceX(g8) = 0.05
    c: Coincident(g4,g8)
    c: DistanceX(g1,g4) = 0.08
    c: DistanceY(g1,g1) = 2
FEATURE [PartDesign::AdditivePipe] AdditivePipe
  AuxilleryCurvelinear = true
  AuxillerySpineTangent = false
  Binormal = (0,0,0)
  Mode = 0
  Placement = pos=(0,0,0) rot=(1,0,0;1.5708rad)
  Profile = -> Sketch010
  Spine = -> Sketch001
  SpineTangent = false
  Transformation = 0
  Transition = 1
FEATURE [PartDesign::Body] Body001  label="Gap"
  Group = -> [Sketch010,AdditivePipe]
  Origin = -> Origin001
  Tip = -> AdditivePipe
COMPONENT P2 — geometry summary ("PO_Top"; no construction recipe available for this part):
  bounding box: 72.3 x 46.3 x 10.3 mm
  tessellated surface: 9,060 triangles
  volume: 7490 mm^3 (22% of its bounding box)
COMPONENT P3 — geometry summary ("PO_Bottom"; no construction recipe available for this part):
  bounding box: 72.3 x 46.3 x 7.8 mm
  tessellated surface: 3,792 triangles
  volume: 10768 mm^3 (41% of its bounding box)
PROVENANCE & LICENSES
A FreeCAD (.FCStd) document from a public repository crawl; recipes are the document's own serialized feature recipes (and, for linked parts, companion documents' recipes).
License: mit.
